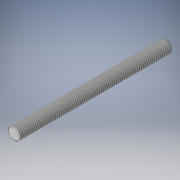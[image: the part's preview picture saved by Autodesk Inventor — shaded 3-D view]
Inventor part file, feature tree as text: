
AUTODESK INVENTOR PART (.ipt)
format: ipt  version: 2017 (Build 210142000, 142)  size: 101,888 bytes
history: native  units: mm
features: chamfer x2, other x1, extrude x1, thread x1, sketch x1
ambient origin geometry x8: Origin, YZ Plane, XZ Plane, XY Plane, X Axis, Y Axis, Z Axis, Center Point
bodies: Body1 (feature_tree)
feature tree (6):
  other  "Твердое тело1"
  extrude  "Выдавливание1"  Depth=8.0mm
  thread  "Резьба1"
  chamfer  "Фаска1"  Distance=100.0mm
  chamfer  "Фаска2"  Distance=0.5mm Angle=45.0deg
  sketch  "Эскиз1"
